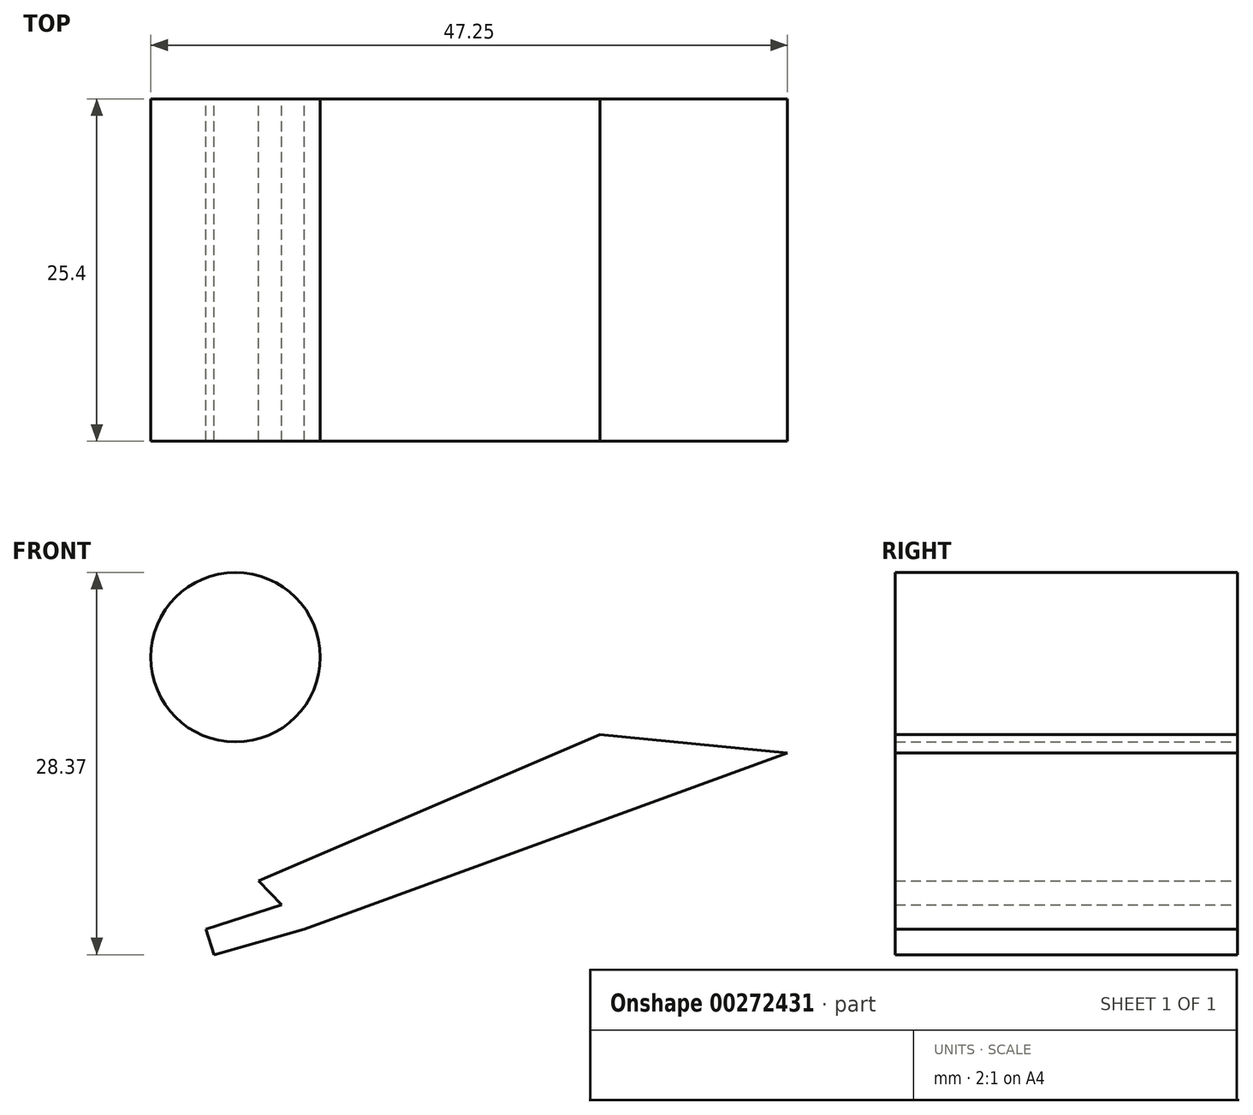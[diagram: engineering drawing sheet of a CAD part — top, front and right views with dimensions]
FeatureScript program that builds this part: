
annotation { "Feature Type Name" : "Feature", "Feature Type Description" : "" }
export const myFeature = defineFeature(function(context is Context, id is Id, definition is map)
    precondition{}
    {
        {
            var Q0;
            Q0=qCreatedBy(makeId("Front.planeOp"),FACE);
            var sketch = newSketch(context, id + "F0", { "sketchPlane" : qUnion([Q0])});
            skCircle(sketch, "E0", {"center": v(-50.51, 30.5) * mm, "radius": 6.3 * mm});
            skLineSegment(sketch, "E1", {"start": v(-48.8, 13.9) * mm, "end": v(-23.48, 24.78) * mm});
            skLineSegment(sketch, "E2", {"start": v(-23.48, 24.78) * mm, "end": v(-9.55, 23.42) * mm});
            skLineSegment(sketch, "E3", {"start": v(-9.55, 23.42) * mm, "end": v(-45.4, 10.34) * mm});
            skLineSegment(sketch, "E4", {"start": v(-45.4, 10.34) * mm, "end": v(-48.8, 13.9) * mm});
            skLineSegment(sketch, "E5", {"start": v(-47.1, 12.12) * mm, "end": v(-52.7, 10.34) * mm});
            skLineSegment(sketch, "E6", {"start": v(-52.7, 10.34) * mm, "end": v(-52.1, 8.43) * mm});
            skLineSegment(sketch, "E7", {"start": v(-52.1, 8.43) * mm, "end": v(-45.4, 10.34) * mm});
            skSolve(sketch);
        }
        {
            var Q0;
            Q0 = qSketchRegion(id + "F0", true);
            extrude(context, id + "F1", {"entities" : qUnion([Q0]), "depth" : 25.4 * mm});
        }
    });
